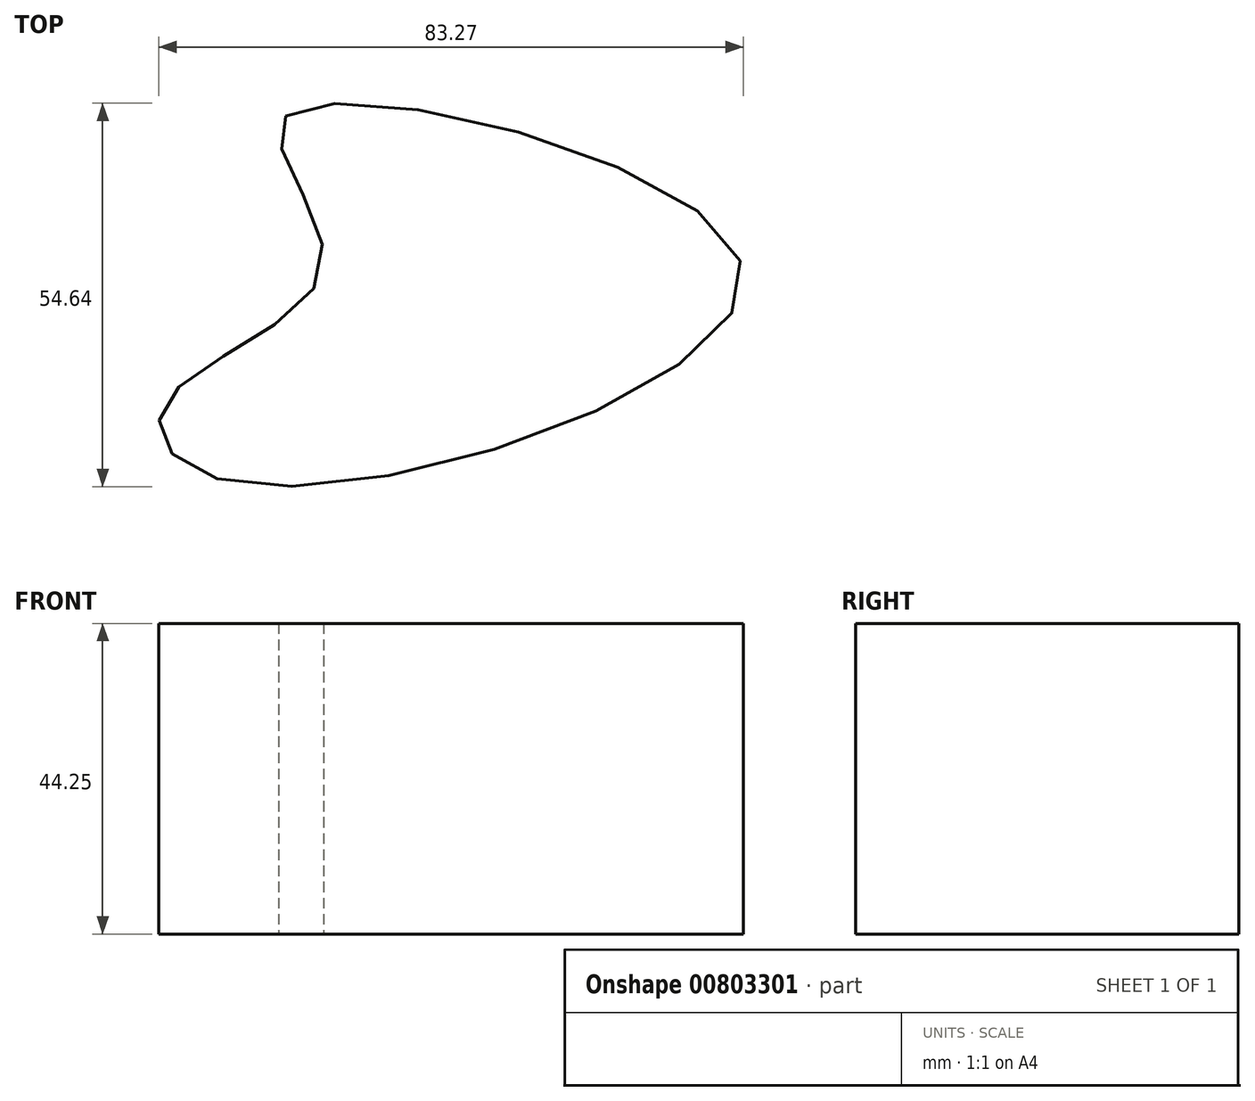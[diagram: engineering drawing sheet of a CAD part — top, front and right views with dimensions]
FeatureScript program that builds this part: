
annotation { "Feature Type Name" : "Feature", "Feature Type Description" : "" }
export const myFeature = defineFeature(function(context is Context, id is Id, definition is map)
    precondition{}
    {
        {
            var Q0;
            Q0=qCreatedBy(makeId("Top.planeOp"),FACE);
            var sketch = newSketch(context, id + "F0", { "sketchPlane" : qUnion([Q0])});
            skFitSpline(sketch, "E0", {"points": [v(-33.42, 66.97) * mm, v(31.53, 45.7) * mm, v(-38.77, 14.42) * mm, v(-50.54, 26.2) * mm, v(-28.08, 45.7) * mm, v(-33.42, 66.97) * mm]});
            skSolve(sketch);
        }
        {
            var Q0;
            Q0=makeQuery(id+"F0.imprint","IMPRINT",FACE,{"disambiguationData":[TD([[makeQuery(id+"F0.imprint","IMPRINT",EDGE,{"derivedFrom":sQuery(id+"F0.wireOp",EDGE,"E0")}),-1.0]])]});
            extrude(context, id + "F1", {"entities" : qUnion([Q0]), "depth" : 44.25 * mm, "offsetDistance" : 25.4 * mm});
        }
        {
            var Q0;
            Q0=qCreatedBy(makeId("Top.planeOp"),FACE);
            var sketch = newSketch(context, id + "F2", { "sketchPlane" : qUnion([Q0])});
            skLineSegment(sketch, "E1", {"start": v(-31.15, -54.63) * mm, "end": v(77.38, -21.39) * mm});
            skSolve(sketch);
        }
        {
            var Q0;
            Q0=sQuery(id+"F2.wireOp",EDGE,"E1");
            extrude(context, id + "F3", {"bodyType" : ToolBodyType.SURFACE, "surfaceEntities" : qUnion([Q0]), "depth" : 22.04 * mm, "offsetDistance" : 25.4 * mm});
        }
    });
